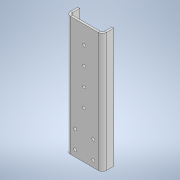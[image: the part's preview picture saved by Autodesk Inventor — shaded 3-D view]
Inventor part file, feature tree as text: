
AUTODESK INVENTOR PART (.ipt)
format: ipt  version: 2022 (Build 260153000, 153)  size: 184,832 bytes
history: native  units: in
note: dims shown in document units (in); Inventor stores cm internally (conversion verified against a paired STEP export)
features: sheet_metal_op x4, other x3, sketch x2, hole x1
ambient origin geometry x8: Origin, YZ Plane, XZ Plane, XY Plane, X Axis, Y Axis, Z Axis, Center Point
bodies: Solid2 (feature_tree)
feature tree (10):
  sketch  "Sketch1"  dims[d0=0.7874in d1=0.7874in]
  sheet_metal_op  "Face1"
  hole  "Hole1"  [1 undecoded]
  sheet_metal_op  "Flange1"
  other  "Plate1"
  sketch  "Sketch2"  dims[d2=0.9843in d3=0.7874in d4=0.2756in d5=0.3937in d6=0.09in d7=0.1339in d8=0.2362in d9=0.2559in d10=0.1181in d11=0.6181in d12=0.09in d13=0.8108in d14=0.09in d15=0.045in d16=0.18in d17=0.09in d18=0.5in d19=90.0deg d20=0.09in d21=0.36in d22=0.09in d23=0.09in]
  other  "Plate2"
  sheet_metal_op  "Bend1"
  sheet_metal_op  "Corner1"
  other  "Definition1"
note: 1 required parameter value undecoded (feature->parameter linkage not recoverable at this tier; creation-order binding heuristic only, values carry confidence <= 0.55)
